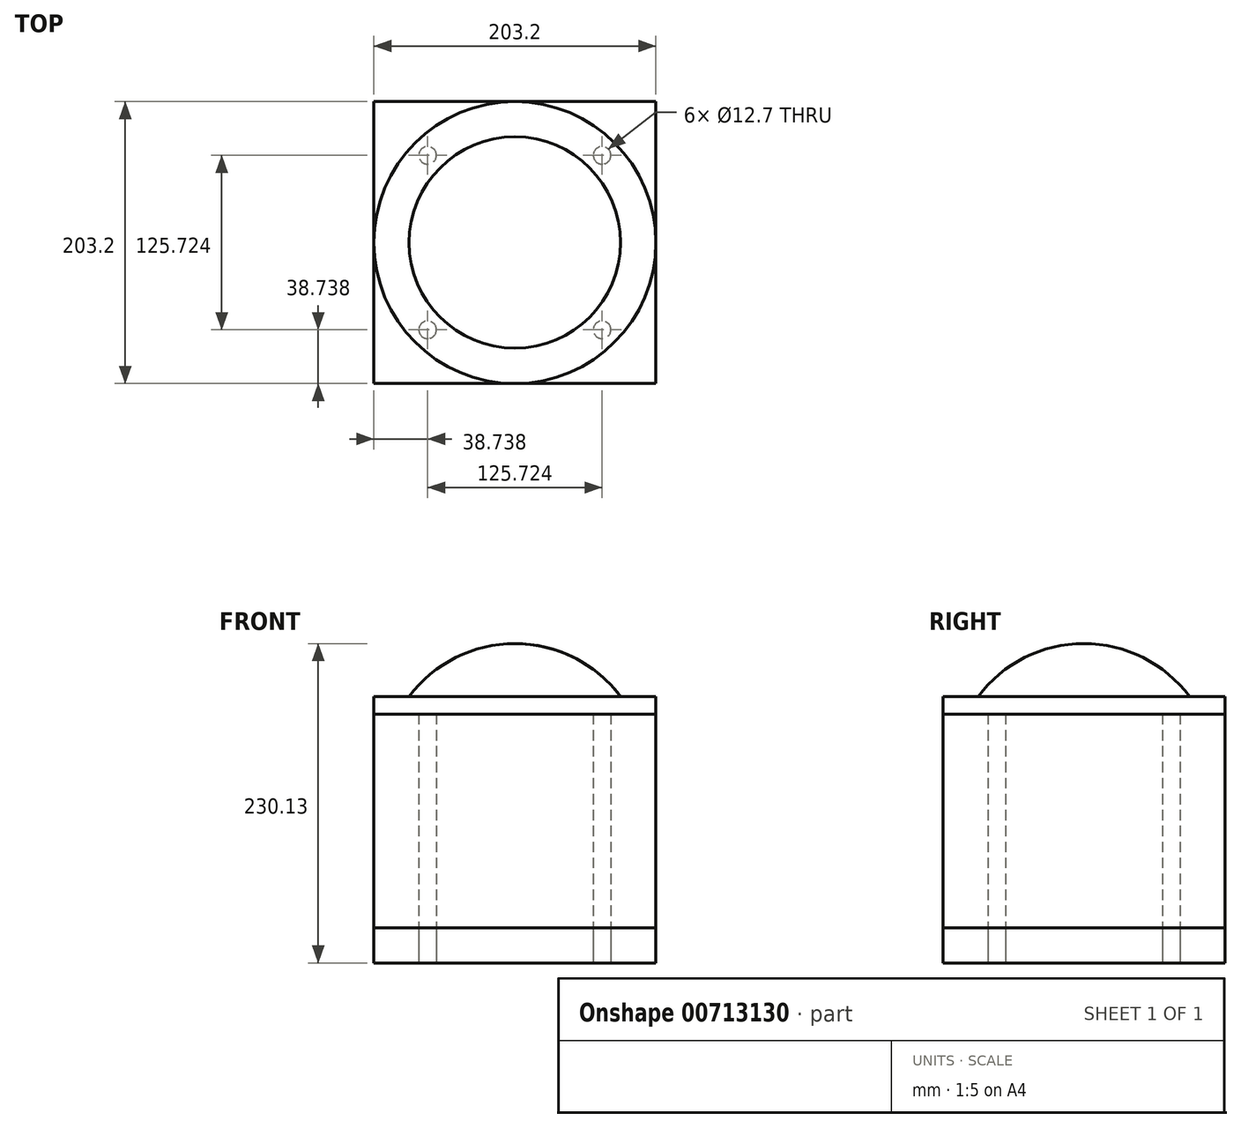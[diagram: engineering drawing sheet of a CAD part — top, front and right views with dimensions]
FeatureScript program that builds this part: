
annotation { "Feature Type Name" : "Feature", "Feature Type Description" : "" }
export const myFeature = defineFeature(function(context is Context, id is Id, definition is map)
    precondition{}
    {
        {
            var Q0;
            Q0=qCreatedBy(makeId("Top.planeOp"),FACE);
            var sketch = newSketch(context, id + "F0", { "sketchPlane" : qUnion([Q0])});
            skLineSegment(sketch, "E0.bottom", {"start": v(-101.6, 101.6) * mm, "end": v(101.6, 101.6) * mm});
            skLineSegment(sketch, "E0.top", {"start": v(-101.6, -101.6) * mm, "end": v(101.6, -101.6) * mm});
            skLineSegment(sketch, "E0.left", {"start": v(-101.6, 101.6) * mm, "end": v(-101.6, -101.6) * mm});
            skLineSegment(sketch, "E0.right", {"start": v(101.6, 101.6) * mm, "end": v(101.6, -101.6) * mm});
            skPoint(sketch, "E0.middle", {"position": v(0, 0) * mm});
            skCircle(sketch, "E1", {"center": v(-62.86, 62.86) * mm, "radius": 6.35 * mm});
            skCircle(sketch, "E2", {"center": v(0, 0) * mm, "radius": 88.9 * mm, "construction": true});
            skLineSegment(sketch, "E3", {"start": v(-101.6, 101.6) * mm, "end": v(101.6, -101.6) * mm, "construction": true});
            skLineSegment(sketch, "E4", {"start": v(0, 101.6) * mm, "end": v(0, -101.6) * mm, "construction": true});
            skLineSegment(sketch, "E5", {"start": v(-101.6, 0) * mm, "end": v(101.6, 0) * mm, "construction": true});
            skLineSegment(sketch, "E6.MirrorCS", {"start": v(101.6, 0) * mm, "end": v(-101.6, 0) * mm, "construction": true});
            skCircle(sketch, "E7.MirrorC", {"center": v(62.86, 62.86) * mm, "radius": 6.35 * mm});
            skCircle(sketch, "E8.MirrorC", {"center": v(-62.86, -62.86) * mm, "radius": 6.35 * mm});
            skCircle(sketch, "E9.MirrorC", {"center": v(62.86, -62.86) * mm, "radius": 6.35 * mm});
            skSolve(sketch);
        }
        {
            var Q0;
            Q0 = qSketchRegion(id + "F0", true);
            extrude(context, id + "F1", {"entities" : qUnion([Q0]), "depth" : 25.4 * mm, "offsetDistance" : 25.4 * mm});
        }
        {
            var Q0;
            Q0=qCreatedBy(makeId("Front.planeOp"),FACE);
            var sketch = newSketch(context, id + "F2", { "sketchPlane" : qUnion([Q0])});
            skLineSegment(sketch, "E10", {"start": v(0, 179.33) * mm, "end": v(-101.6, 179.33) * mm});
            skLineSegment(sketch, "E11", {"start": v(-101.6, 179.33) * mm, "end": v(-101.6, 192.03) * mm});
            skLineSegment(sketch, "E12", {"start": v(-101.6, 192.03) * mm, "end": v(-76.2, 192.03) * mm});
            skLineSegment(sketch, "E13", {"start": v(0, 179.33) * mm, "end": v(0, 230.13) * mm});
            skArc(sketch, "E14", {"start": v(0, 230.13) * mm, "mid": v(-42.6, 220.07) * mm, "end": v(-76.2, 192.03) * mm});
            skSolve(sketch);
        }
        {
            var Q0;
            Q0=makeQuery(id+"F2.imprint","IMPRINT",FACE,{"disambiguationData":[TD([[makeQuery(id+"F2.imprint","IMPRINT",EDGE,{"derivedFrom":sQuery(id+"F2.wireOp",EDGE,"E10")}),-1.0]])]});
            var Q1;
            Q1=sQuery(id+"F2.wireOp",EDGE,"E13");
            revolve(context, id + "F3", {"surfaceOperationType" : NewSurfaceOperationType.NEW, "entities" : qUnion([Q0]), "axis" : qUnion([Q1]), "revolveType" : RevolveType.FULL});
        }
        {
            var Q0;
            Q0=makeQuery(id+"F0.imprint","IMPRINT",FACE,{"disambiguationData":[TD([[makeQuery(id+"F0.imprint","IMPRINT",EDGE,{"derivedFrom":sQuery(id+"F0.wireOp",EDGE,"E9.MirrorC")}),1.0]])]});
            var Q1;
            Q1=makeQuery(id+"F0.imprint","IMPRINT",FACE,{"disambiguationData":[TD([[makeQuery(id+"F0.imprint","IMPRINT",EDGE,{"derivedFrom":sQuery(id+"F0.wireOp",EDGE,"E7.MirrorC")}),-1.0]])]});
            var Q2;
            Q2=makeQuery(id+"F0.imprint","IMPRINT",FACE,{"disambiguationData":[TD([[makeQuery(id+"F0.imprint","IMPRINT",EDGE,{"derivedFrom":sQuery(id+"F0.wireOp",EDGE,"E1")}),1.0]])]});
            var Q3;
            Q3=makeQuery(id+"F0.imprint","IMPRINT",FACE,{"disambiguationData":[TD([[makeQuery(id+"F0.imprint","IMPRINT",EDGE,{"derivedFrom":sQuery(id+"F0.wireOp",EDGE,"E8.MirrorC")}),-1.0]])]});
            var Q4;
            Q4=sQuery(id+"F0.wireOp",EDGE,"E8.MirrorC");
            var Q5;
            Q5=sQuery(id+"F0.wireOp",EDGE,"E9.MirrorC");
            var Q6;
            Q6=sQuery(id+"F0.wireOp",EDGE,"E7.MirrorC");
            var Q7;
            Q7=sQuery(id+"F0.wireOp",EDGE,"E1");
            var Q8;
            Q8=makeQuery(id+"F3.opRevolve","SWEPT_FACE",FACE,{"disambiguationData":[OSD([sQuery(id+"F2.wireOp",EDGE,"E10")])]});
            extrude(context, id + "F4", {"entities" : qUnion([Q0, Q1, Q2, Q3]), "surfaceEntities" : qUnion([Q4, Q5, Q6, Q7]), "endBound" : BoundingType.UP_TO_SURFACE, "depth" : 177.8 * mm, "endBoundEntityFace" : qUnion([Q8]), "offsetDistance" : 25.4 * mm});
        }
    });
